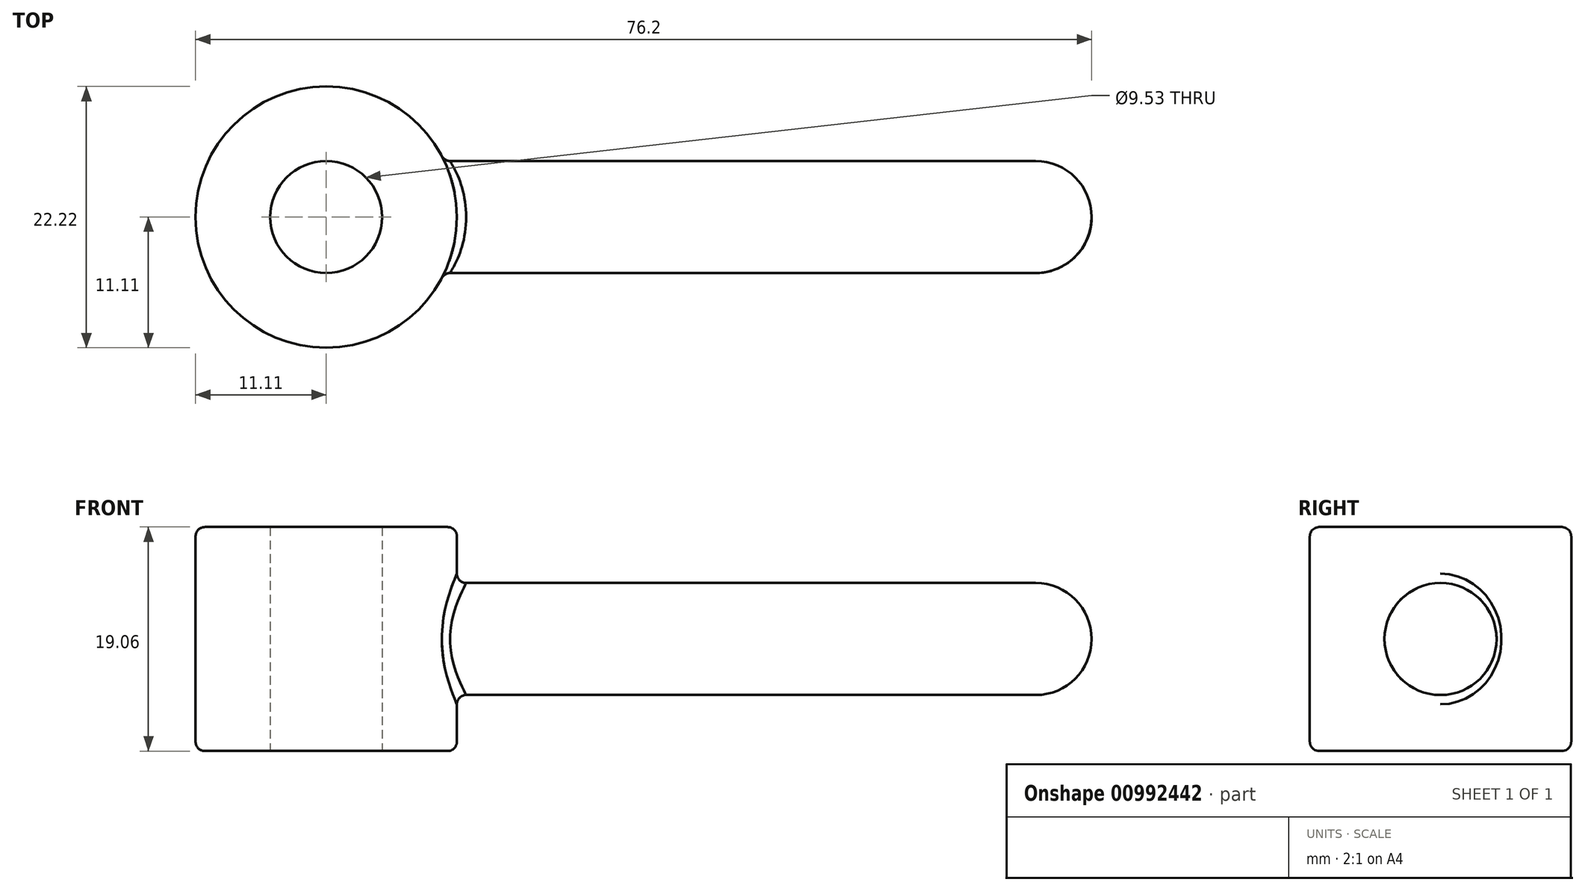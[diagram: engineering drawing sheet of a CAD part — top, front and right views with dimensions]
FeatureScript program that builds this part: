
annotation { "Feature Type Name" : "Feature", "Feature Type Description" : "" }
export const myFeature = defineFeature(function(context is Context, id is Id, definition is map)
    precondition{}
    {
        {
            var Q0;
            Q0=qCreatedBy(makeId("Top.planeOp"),FACE);
            var sketch = newSketch(context, id + "F0", { "sketchPlane" : qUnion([Q0])});
            skCircle(sketch, "E0", {"center": v(-38.1, 0) * mm, "radius": 4.76 * mm});
            skCircle(sketch, "E1", {"center": v(-38.1, 0) * mm, "radius": 11.11 * mm});
            skLineSegment(sketch, "E2.bottom", {"start": v(-38.1, -4.76) * mm, "end": v(22.23, -4.76) * mm});
            skLineSegment(sketch, "E2.top", {"start": v(-38.1, 4.76) * mm, "end": v(22.23, 4.76) * mm});
            skLineSegment(sketch, "E2.left", {"start": v(-38.1, -4.76) * mm, "end": v(-38.1, 4.76) * mm});
            skArc(sketch, "E3", {"start": v(22.23, -4.76) * mm, "mid": v(26.99, 0) * mm, "end": v(22.22, 4.76) * mm});
            skPoint(sketch, "E3.centerSnap0", {"position": v(26.99, 0) * mm});
            skLineSegment(sketch, "E4", {"start": v(-49.21, 0) * mm, "end": v(26.99, 0) * mm});
            skSolve(sketch);
        }
        {
            var Q0;
            {var subQ3=sQuery(id+"F0.wireOp",EDGE,"E4");var subQ5=sQuery(id+"F0.wireOp",EDGE,"E1");var subQ6=makeQuery(id+"F0.imprint","INTERSECT",VERTEX,{"disambiguationData":[OD(0.0)],"derivedFrom":[subQ5,subQ3]});Q0=makeQuery(id+"F0.imprint","IMPRINT",FACE,{"disambiguationData":[TD([[makeQuery(id+"F0.imprint","IMPRINT",EDGE,{"disambiguationData":[TD([[subQ6,1.0]])],"derivedFrom":subQ5}),1.0]])]});}
            var Q1;
            {var subQ3=sQuery(id+"F0.wireOp",EDGE,"E4");var subQ5=sQuery(id+"F0.wireOp",EDGE,"E1");var subQ6=makeQuery(id+"F0.imprint","INTERSECT",VERTEX,{"disambiguationData":[OD(0.0)],"derivedFrom":[subQ5,subQ3]});Q1=makeQuery(id+"F0.imprint","IMPRINT",FACE,{"disambiguationData":[TD([[makeQuery(id+"F0.imprint","IMPRINT",EDGE,{"disambiguationData":[TD([[subQ6,-1.0]])],"derivedFrom":subQ5}),1.0]])]});}
            var Q2;
            {var subQ0=sQuery(id+"F0.wireOp",EDGE,"E2.bottom");var subQ5=sQuery(id+"F0.wireOp",EDGE,"E1");var subQ6=makeQuery(id+"F0.imprint","INTERSECT",VERTEX,{"derivedFrom":[subQ5,subQ0]});Q2=makeQuery(id+"F0.imprint","IMPRINT",FACE,{"disambiguationData":[TD([[makeQuery(id+"F0.imprint","IMPRINT",EDGE,{"disambiguationData":[TD([[subQ6,-1.0]])],"derivedFrom":subQ5}),1.0]])]});}
            var Q3;
            {var subQ0=sQuery(id+"F0.wireOp",EDGE,"E2.top");var subQ5=sQuery(id+"F0.wireOp",EDGE,"E1");var subQ6=makeQuery(id+"F0.imprint","INTERSECT",VERTEX,{"derivedFrom":[subQ5,subQ0]});Q3=makeQuery(id+"F0.imprint","IMPRINT",FACE,{"disambiguationData":[TD([[makeQuery(id+"F0.imprint","IMPRINT",EDGE,{"disambiguationData":[TD([[subQ6,1.0]])],"derivedFrom":subQ5}),1.0]])]});}
            extrude(context, id + "F1", {"entities" : qUnion([Q0, Q1, Q2, Q3]), "depth" : 19.05 * mm, "offsetDistance" : 25.4 * mm, "symmetric" : true});
        }
        {
            var Q0;
            {var subQ0=sQuery(id+"F0.wireOp",EDGE,"E2.top");var subQ1=sQuery(id+"F0.wireOp",EDGE,"E1");var subQ2=makeQuery(id+"F0.imprint","INTERSECT",VERTEX,{"derivedFrom":[subQ1,subQ0]});Q0=makeQuery(id+"F0.imprint","IMPRINT",FACE,{"disambiguationData":[TD([[makeQuery(id+"F0.imprint","IMPRINT",EDGE,{"disambiguationData":[TD([[subQ2,1.0]])],"derivedFrom":subQ1}),-1.0]])]});}
            var Q1;
            Q1=sQuery(id+"F0.wireOp",EDGE,"E4");
            revolve(context, id + "F2", {"operationType" : NewBodyOperationType.ADD, "surfaceOperationType" : NewSurfaceOperationType.NEW, "entities" : qUnion([Q0]), "axis" : qUnion([Q1]), "revolveType" : RevolveType.FULL});
        }
        {
            var Q0;
            Q0=makeQuery(id+"F1.opExtrude","CAP_EDGE",EDGE,{"disambiguationData":[OSD([sQuery(id+"F0.wireOp",EDGE,"E1")])],"isStart":false});
            var Q1;
            Q1=makeQuery(id+"F1.opExtrude","CAP_EDGE",EDGE,{"disambiguationData":[OSD([sQuery(id+"F0.wireOp",EDGE,"E1")])],"isStart":true});
            var Q2;
            Q2=makeQuery(id+"F2.boolean.opBoolean","INTERSECT",EDGE,{"derivedFrom":[makeQuery(id+"F1.opExtrude","SWEPT_FACE",FACE,{"disambiguationData":[OSD([sQuery(id+"F0.wireOp",EDGE,"E1")])]}),makeQuery(id+"F2.opRevolve","SWEPT_FACE",FACE,{"disambiguationData":[OSD([sQuery(id+"F0.wireOp",EDGE,"E2.top")])]})]});
            fillet(context, id + "F3", {"entities" : qUnion([Q0, Q1, Q2]), "radius" : 0.8 * mm, "tangentPropagation" : true, "allowEdgeOverflow" : false});
        }
    });
